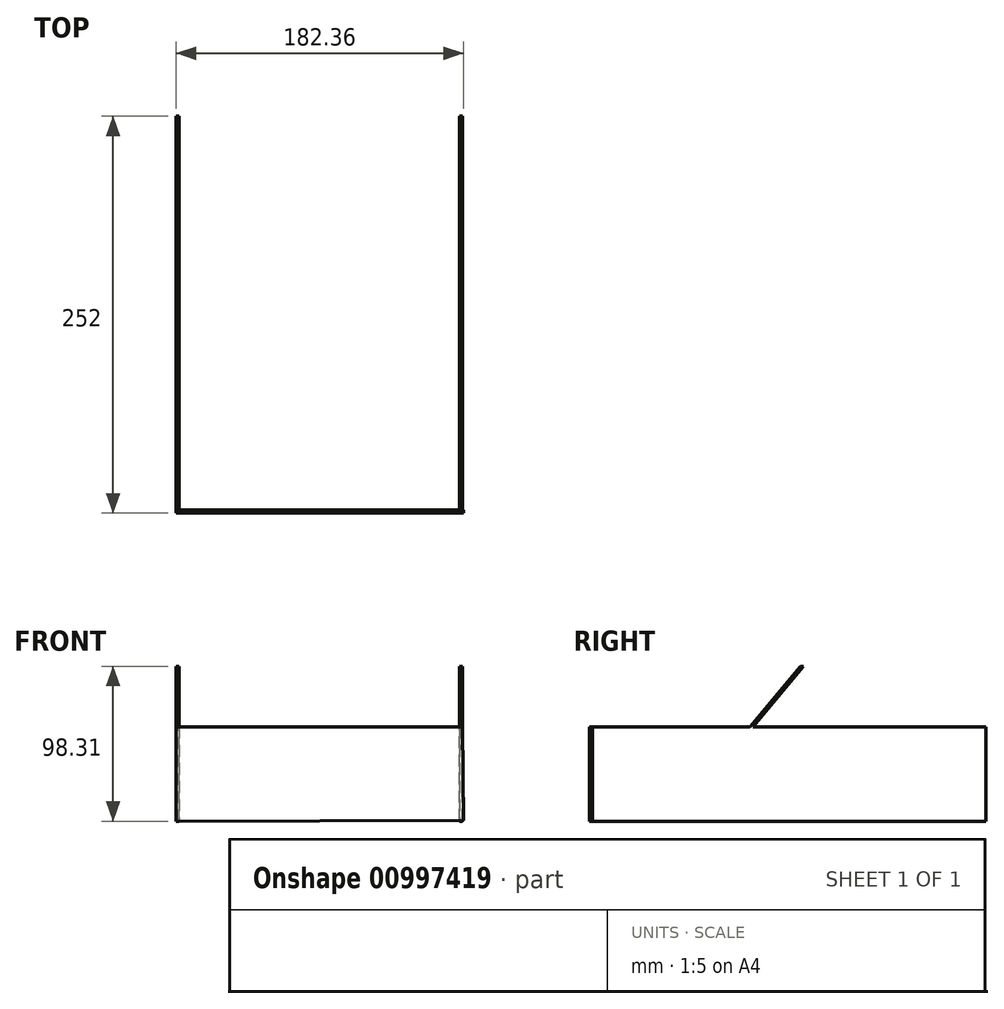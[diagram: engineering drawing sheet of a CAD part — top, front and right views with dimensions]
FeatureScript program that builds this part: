
annotation { "Feature Type Name" : "Feature", "Feature Type Description" : "" }
export const myFeature = defineFeature(function(context is Context, id is Id, definition is map)
    precondition{}
    {
        {
            var Q0;
            Q0=qCreatedBy(makeId("Right.planeOp"),FACE);
            var sketch = newSketch(context, id + "F0", { "sketchPlane" : qUnion([Q0])});
            skLineSegment(sketch, "E0", {"start": v(-171.52, -77.44) * mm, "end": v(-171.52, -17.44) * mm});
            skLineSegment(sketch, "E1", {"start": v(-171.52, -17.44) * mm, "end": v(-71.52, -17.44) * mm});
            skLineSegment(sketch, "E2", {"start": v(-71.52, -17.44) * mm, "end": v(-39.38, 20.87) * mm});
            skLineSegment(sketch, "E3", {"start": v(-39.38, 20.87) * mm, "end": v(-37.38, 20.87) * mm});
            skLineSegment(sketch, "E4", {"start": v(-37.38, 20.87) * mm, "end": v(-69.52, -17.44) * mm});
            skLineSegment(sketch, "E5", {"start": v(-69.52, -17.44) * mm, "end": v(78.48, -17.44) * mm});
            skLineSegment(sketch, "E6", {"start": v(78.48, -17.44) * mm, "end": v(78.48, -77.44) * mm});
            skLineSegment(sketch, "E7", {"start": v(78.48, -77.44) * mm, "end": v(-171.52, -77.44) * mm});
            skSolve(sketch);
        }
        {
            var Q0;
            Q0=makeQuery(id+"F0.imprint","IMPRINT",FACE,{"disambiguationData":[TD([[makeQuery(id+"F0.imprint","IMPRINT",EDGE,{"derivedFrom":sQuery(id+"F0.wireOp",EDGE,"E0")}),-1.0]])]});
            extrude(context, id + "F1", {"entities" : qUnion([Q0]), "depth" : 2 * mm, "offsetDistance" : 25 * mm});
        }
        {
            var Q0;
            Q0=makeQuery(id+"F1.opExtrude","SWEPT_BODY",BODY,{"disambiguationData":[OSD([sQuery(id+"F0.wireOp",EDGE,"E0"),sQuery(id+"F0.wireOp",EDGE,"E1"),sQuery(id+"F0.wireOp",EDGE,"E2"),sQuery(id+"F0.wireOp",EDGE,"E3"),sQuery(id+"F0.wireOp",EDGE,"E4"),sQuery(id+"F0.wireOp",EDGE,"E5"),sQuery(id+"F0.wireOp",EDGE,"E6"),sQuery(id+"F0.wireOp",EDGE,"E7")])]});
            transform(context, id + "F2", {"entities" : qUnion([Q0]), "transformType" : TransformType.TRANSLATION_3D, "dx" : -180 * mm, "dy" : 0 * mm, "dz" : 0 * mm, "makeCopy" : true});
        }
        {
            var Q0;
            Q0=makeQuery(id+"F2.opPattern","COPY",FACE,{"derivedFrom":makeQuery(id+"F1.opExtrude","SWEPT_FACE",FACE,{"disambiguationData":[OSD([sQuery(id+"F0.wireOp",EDGE,"E0")])]}),"instanceName":"1"});
            var sketch = newSketch(context, id + "F3", { "sketchPlane" : qUnion([Q0])});
            skLineSegment(sketch, "E8", {"start": v(-180, -17.44) * mm, "end": v(2, -17.44) * mm});
            skLineSegment(sketch, "E9", {"start": v(2, -17.44) * mm, "end": v(2.36, -77) * mm});
            skLineSegment(sketch, "E10", {"start": v(-180, -17.44) * mm, "end": v(-180, -77.44) * mm});
            skLineSegment(sketch, "E11", {"start": v(-180, -77.44) * mm, "end": v(2.36, -77) * mm});
            skSolve(sketch);
        }
        {
            var Q0;
            {var subQ0=sQuery(id+"F3.wireOp",EDGE,"E10");Q0=makeQuery(id+"F3.imprint","IMPRINT",FACE,{"disambiguationData":[TD([[makeQuery(id+"F3.imprint","IMPRINT",EDGE,{"derivedFrom":subQ0}),-1.0]])]});}
            var Q1;
            {var subQ3=sQuery(id+"F3.wireOp",EDGE,"E9");Q1=makeQuery(id+"F3.imprint","IMPRINT",FACE,{"disambiguationData":[TD([[makeQuery(id+"F3.imprint","IMPRINT",EDGE,{"derivedFrom":subQ3}),-1.0]])]});}
            extrude(context, id + "F4", {"entities" : qUnion([Q0, Q1]), "depth" : 2 * mm, "offsetDistance" : 25 * mm});
        }
    });
